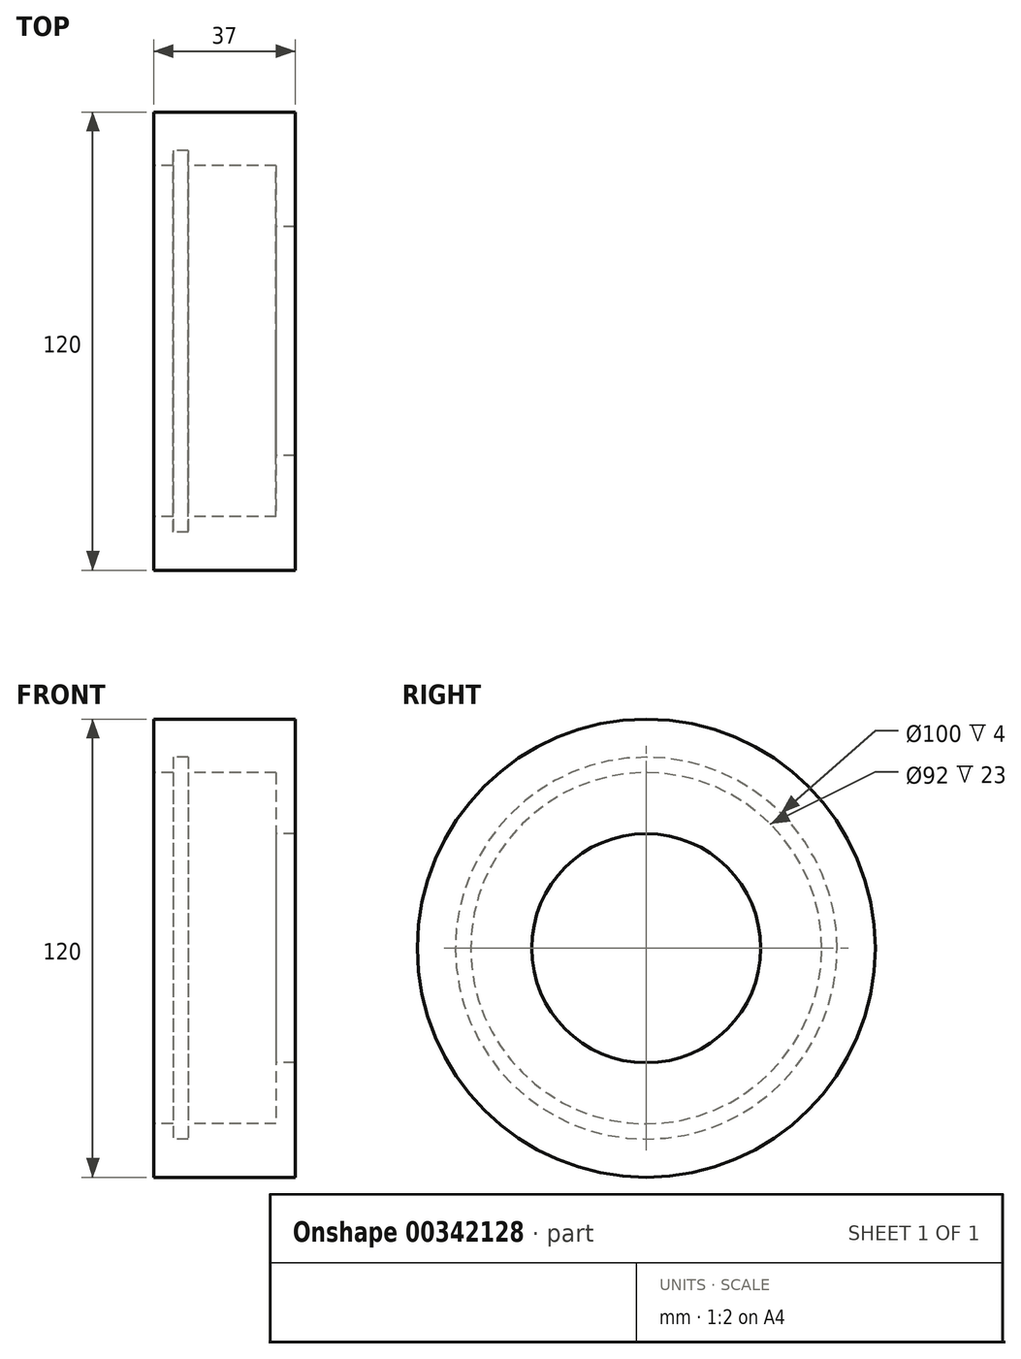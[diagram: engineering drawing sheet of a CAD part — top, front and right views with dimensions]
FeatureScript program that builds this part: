
annotation { "Feature Type Name" : "Feature", "Feature Type Description" : "" }
export const myFeature = defineFeature(function(context is Context, id is Id, definition is map)
    precondition{}
    {
        {
            var Q0;
            Q0=qCreatedBy(makeId("Front.planeOp"),FACE);
            var sketch = newSketch(context, id + "F0", { "sketchPlane" : qUnion([Q0])});
            skLineSegment(sketch, "E0", {"start": v(-113.8, 0) * mm, "end": v(125.75, 0) * mm});
            skLineSegment(sketch, "E1.bottom", {"start": v(-32, 0) * mm, "end": v(5, 0) * mm});
            skLineSegment(sketch, "E1.top", {"start": v(-32, 60) * mm, "end": v(5, 60) * mm});
            skLineSegment(sketch, "E1.left", {"start": v(-32, 0) * mm, "end": v(-32, 60) * mm});
            skLineSegment(sketch, "E1.right", {"start": v(5, 0) * mm, "end": v(5, 60) * mm});
            skLineSegment(sketch, "E2", {"start": v(0, 46) * mm, "end": v(0, 0) * mm});
            skLineSegment(sketch, "E3", {"start": v(0, 30) * mm, "end": v(5, 30) * mm});
            skLineSegment(sketch, "E4", {"start": v(-32, 46) * mm, "end": v(-27, 46) * mm});
            skLineSegment(sketch, "E5", {"start": v(-27, 46) * mm, "end": v(-27, 50) * mm});
            skLineSegment(sketch, "E6", {"start": v(-27, 50) * mm, "end": v(-23, 50) * mm});
            skLineSegment(sketch, "E7", {"start": v(-23, 50) * mm, "end": v(-23, 46) * mm});
            skLineSegment(sketch, "E8", {"start": v(-23, 46) * mm, "end": v(0, 46) * mm});
            skLineSegment(sketch, "E9", {"start": v(-27, 46) * mm, "end": v(-27, 0) * mm});
            skLineSegment(sketch, "E10", {"start": v(-23, 46) * mm, "end": v(-23, 0) * mm});
            skSolve(sketch);
        }
        {
            var Q0;
            {var subQ1=sQuery(id+"F0.wireOp",EDGE,"E1.top");Q0=makeQuery(id+"F0.imprint","IMPRINT",FACE,{"disambiguationData":[TD([[makeQuery(id+"F0.imprint","IMPRINT",EDGE,{"derivedFrom":subQ1}),-1.0]])]});}
            var Q1;
            Q1=sQuery(id+"F0.wireOp",EDGE,"E0");
            revolve(context, id + "F1", {"entities" : qUnion([Q0]), "axis" : qUnion([Q1]), "revolveType" : RevolveType.FULL});
        }
    });
